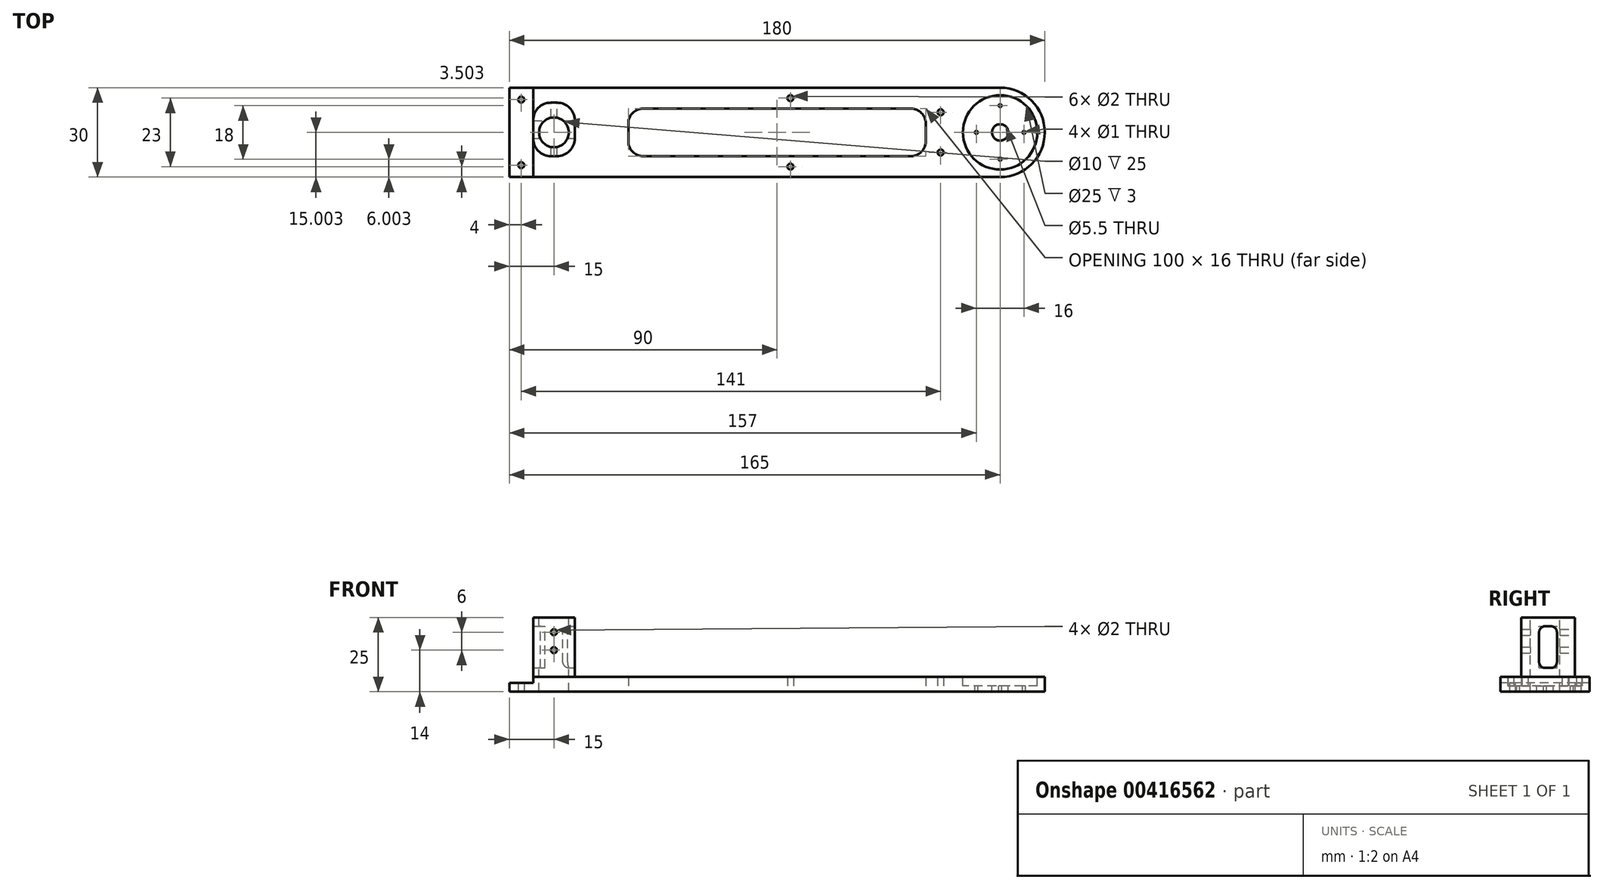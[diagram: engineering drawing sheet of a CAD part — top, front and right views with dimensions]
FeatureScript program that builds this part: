
annotation { "Feature Type Name" : "Feature", "Feature Type Description" : "" }
export const myFeature = defineFeature(function(context is Context, id is Id, definition is map)
    precondition{}
    {
        {
            var Q0;
            Q0=qCreatedBy(makeId("Top.planeOp"),FACE);
            var sketch = newSketch(context, id + "F0", { "sketchPlane" : qUnion([Q0])});
            skLineSegment(sketch, "E0.bottom", {"start": v(-80, 3.1) * mm, "end": v(100, 3.1) * mm});
            skLineSegment(sketch, "E0.top", {"start": v(-80, -26.9) * mm, "end": v(100, -26.9) * mm});
            skLineSegment(sketch, "E0.left", {"start": v(-80, 3.1) * mm, "end": v(-80, -26.9) * mm});
            skLineSegment(sketch, "E0.right", {"start": v(100, 3.1) * mm, "end": v(100, -26.9) * mm});
            skCircle(sketch, "E1", {"center": v(65, -5.15) * mm, "radius": 1 * mm});
            skCircle(sketch, "E2", {"center": v(65, -18.65) * mm, "radius": 1 * mm});
            skLineSegment(sketch, "E3.bottom", {"start": v(-40, -3.9) * mm, "end": v(60, -3.9) * mm});
            skLineSegment(sketch, "E3.top", {"start": v(-40, -19.9) * mm, "end": v(60, -19.9) * mm});
            skLineSegment(sketch, "E3.left", {"start": v(-40, -3.9) * mm, "end": v(-40, -19.9) * mm});
            skLineSegment(sketch, "E3.right", {"start": v(60, -3.9) * mm, "end": v(60, -19.9) * mm});
            skCircle(sketch, "E4", {"center": v(-76, -0.9) * mm, "radius": 1 * mm});
            skCircle(sketch, "E5", {"center": v(-76, -22.9) * mm, "radius": 1 * mm});
            skCircle(sketch, "E6", {"center": v(14.5, -23.4) * mm, "radius": 1 * mm});
            skCircle(sketch, "E7", {"center": v(14.5, -0.4) * mm, "radius": 1 * mm});
            skSolve(sketch);
        }
        {
            var Q0;
            Q0=makeQuery(id+"F0.imprint","IMPRINT",FACE,{"disambiguationData":[TD([[makeQuery(id+"F0.imprint","IMPRINT",EDGE,{"derivedFrom":sQuery(id+"F0.wireOp",EDGE,"E0.bottom")}),-1.0]])]});
            extrude(context, id + "F1", {"entities" : qUnion([Q0]), "depth" : 5 * mm});
        }
        {
            var Q0;
            Q0=makeQuery(id+"F1.opExtrude","CAP_FACE",FACE,{"disambiguationData":[OSD([sQuery(id+"F0.wireOp",EDGE,"E0.bottom"),sQuery(id+"F0.wireOp",EDGE,"E0.top"),sQuery(id+"F0.wireOp",EDGE,"E0.left"),sQuery(id+"F0.wireOp",EDGE,"E0.right")])],"isStart":false});
            var sketch = newSketch(context, id + "F2", { "sketchPlane" : qUnion([Q0])});
            skCircle(sketch, "E8", {"center": v(85, -11.9) * mm, "radius": 12.5 * mm});
            skCircle(sketch, "E9", {"center": v(85, -11.9) * mm, "radius": 2.75 * mm});
            skCircle(sketch, "E10", {"center": v(85, -2.9) * mm, "radius": 0.5 * mm});
            skCircle(sketch, "E11", {"center": v(85, -20.9) * mm, "radius": 0.5 * mm});
            skCircle(sketch, "E12", {"center": v(93, -11.9) * mm, "radius": 0.5 * mm});
            skCircle(sketch, "E13", {"center": v(77, -11.9) * mm, "radius": 0.5 * mm});
            skCircle(sketch, "E14", {"center": v(-65, -11.9) * mm, "radius": 5 * mm});
            skLineSegment(sketch, "E15.bottom", {"start": v(-72, -1.9) * mm, "end": v(-58, -1.9) * mm});
            skLineSegment(sketch, "E15.top", {"start": v(-72, -19.9) * mm, "end": v(-58, -19.9) * mm});
            skLineSegment(sketch, "E15.left", {"start": v(-72, -1.9) * mm, "end": v(-72, -19.9) * mm});
            skLineSegment(sketch, "E15.right", {"start": v(-58, -1.9) * mm, "end": v(-58, -19.9) * mm});
            skLineSegment(sketch, "E16.bottom", {"start": v(-80, 3.1) * mm, "end": v(-72, 3.1) * mm});
            skLineSegment(sketch, "E16.top", {"start": v(-80, -26.9) * mm, "end": v(-72, -26.9) * mm});
            skLineSegment(sketch, "E16.left", {"start": v(-80, 3.1) * mm, "end": v(-80, -26.9) * mm});
            skLineSegment(sketch, "E16.right", {"start": v(-72, 3.1) * mm, "end": v(-72, -26.9) * mm});
            skSolve(sketch);
        }
        {
            var Q0;
            Q0=makeQuery(id+"F2.imprint","IMPRINT",FACE,{"disambiguationData":[TD([[makeQuery(id+"F2.imprint","IMPRINT",EDGE,{"derivedFrom":sQuery(id+"F2.wireOp",EDGE,"E8")}),1.0]])]});
            extrude(context, id + "F3", {"entities" : qUnion([Q0]), "operationType" : NewBodyOperationType.REMOVE, "oppositeDirection" : true, "depth" : 3 * mm});
        }
        {
            var Q0;
            Q0=makeQuery(id+"F2.imprint","IMPRINT",FACE,{"disambiguationData":[TD([[makeQuery(id+"F2.imprint","IMPRINT",EDGE,{"derivedFrom":sQuery(id+"F2.wireOp",EDGE,"E9")}),1.0]])]});
            var Q1;
            Q1=makeQuery(id+"F2.imprint","IMPRINT",FACE,{"disambiguationData":[TD([[makeQuery(id+"F2.imprint","IMPRINT",EDGE,{"derivedFrom":sQuery(id+"F2.wireOp",EDGE,"E10")}),1.0]])]});
            var Q2;
            Q2=makeQuery(id+"F2.imprint","IMPRINT",FACE,{"disambiguationData":[TD([[makeQuery(id+"F2.imprint","IMPRINT",EDGE,{"derivedFrom":sQuery(id+"F2.wireOp",EDGE,"E13")}),1.0]])]});
            var Q3;
            Q3=makeQuery(id+"F2.imprint","IMPRINT",FACE,{"disambiguationData":[TD([[makeQuery(id+"F2.imprint","IMPRINT",EDGE,{"derivedFrom":sQuery(id+"F2.wireOp",EDGE,"E11")}),1.0]])]});
            var Q4;
            Q4=makeQuery(id+"F2.imprint","IMPRINT",FACE,{"disambiguationData":[TD([[makeQuery(id+"F2.imprint","IMPRINT",EDGE,{"derivedFrom":sQuery(id+"F2.wireOp",EDGE,"E12")}),1.0]])]});
            extrude(context, id + "F4", {"entities" : qUnion([Q0, Q1, Q2, Q3, Q4]), "operationType" : NewBodyOperationType.REMOVE, "oppositeDirection" : true, "depth" : 25 * mm});
        }
        {
            var Q0;
            Q0=makeQuery(id+"F1.opExtrude","SWEPT_EDGE",EDGE,{"disambiguationData":[OSD([sQuery(id+"F0.wireOp",EDGE,"E0.bottom"),sQuery(id+"F0.wireOp",EDGE,"E0.right")])]});
            var Q1;
            Q1=makeQuery(id+"F1.opExtrude","SWEPT_EDGE",EDGE,{"disambiguationData":[OSD([sQuery(id+"F0.wireOp",EDGE,"E0.top"),sQuery(id+"F0.wireOp",EDGE,"E0.right")])]});
            fillet(context, id + "F5", {"entities" : qUnion([Q0, Q1]), "radius" : 15 * mm, "tangentPropagation" : true, "allowEdgeOverflow" : false});
        }
        {
            var Q0;
            Q0=makeQuery(id+"F2.imprint","IMPRINT",FACE,{"disambiguationData":[TD([[makeQuery(id+"F2.imprint","IMPRINT",EDGE,{"derivedFrom":sQuery(id+"F2.wireOp",EDGE,"E14")}),1.0]])]});
            extrude(context, id + "F6", {"entities" : qUnion([Q0]), "operationType" : NewBodyOperationType.REMOVE, "oppositeDirection" : true, "depth" : 25 * mm});
        }
        {
            var Q0;
            Q0=makeQuery(id+"F1.opExtrude","SWEPT_EDGE",EDGE,{"disambiguationData":[OSD([sQuery(id+"F0.wireOp",EDGE,"E3.bottom"),sQuery(id+"F0.wireOp",EDGE,"E3.left")])]});
            var Q1;
            Q1=makeQuery(id+"F1.opExtrude","SWEPT_EDGE",EDGE,{"disambiguationData":[OSD([sQuery(id+"F0.wireOp",EDGE,"E3.top"),sQuery(id+"F0.wireOp",EDGE,"E3.left")])]});
            var Q2;
            Q2=makeQuery(id+"F1.opExtrude","SWEPT_EDGE",EDGE,{"disambiguationData":[OSD([sQuery(id+"F0.wireOp",EDGE,"E3.bottom"),sQuery(id+"F0.wireOp",EDGE,"E3.right")])]});
            var Q3;
            Q3=makeQuery(id+"F1.opExtrude","SWEPT_EDGE",EDGE,{"disambiguationData":[OSD([sQuery(id+"F0.wireOp",EDGE,"E3.top"),sQuery(id+"F0.wireOp",EDGE,"E3.right")])]});
            fillet(context, id + "F7", {"entities" : qUnion([Q0, Q1, Q2, Q3]), "radius" : 5 * mm, "tangentPropagation" : true, "allowEdgeOverflow" : false});
        }
        {
            var Q0;
            Q0=makeQuery(id+"F2.imprint","IMPRINT",FACE,{"disambiguationData":[TD([[makeQuery(id+"F2.imprint","IMPRINT",EDGE,{"derivedFrom":sQuery(id+"F2.wireOp",EDGE,"E14")}),-1.0]])]});
            extrude(context, id + "F8", {"entities" : qUnion([Q0]), "operationType" : NewBodyOperationType.ADD, "depth" : 20 * mm, "offsetDistance" : 25 * mm});
        }
        {
            var Q0;
            Q0=makeQuery(id+"F8.opExtrude","SWEPT_EDGE",EDGE,{"disambiguationData":[OSD([sQuery(id+"F2.wireOp",EDGE,"E15.top"),sQuery(id+"F2.wireOp",EDGE,"E15.left")])]});
            var Q1;
            Q1=makeQuery(id+"F8.opExtrude","SWEPT_EDGE",EDGE,{"disambiguationData":[OSD([sQuery(id+"F2.wireOp",EDGE,"E15.top"),sQuery(id+"F2.wireOp",EDGE,"E15.right")])]});
            var Q2;
            Q2=makeQuery(id+"F8.opExtrude","SWEPT_EDGE",EDGE,{"disambiguationData":[OSD([sQuery(id+"F2.wireOp",EDGE,"E15.bottom"),sQuery(id+"F2.wireOp",EDGE,"E15.left")])]});
            var Q3;
            Q3=makeQuery(id+"F8.opExtrude","SWEPT_EDGE",EDGE,{"disambiguationData":[OSD([sQuery(id+"F2.wireOp",EDGE,"E15.bottom"),sQuery(id+"F2.wireOp",EDGE,"E15.right")])]});
            fillet(context, id + "F9", {"entities" : qUnion([Q0, Q1, Q2, Q3]), "radius" : 6 * mm, "tangentPropagation" : true, "allowEdgeOverflow" : false});
        }
        {
            var Q0;
            {var subQ2=sQuery(id+"F2.wireOp",EDGE,"E16.bottom");Q0=makeQuery(id+"F2.imprint","IMPRINT",FACE,{"disambiguationData":[TD([[makeQuery(id+"F2.imprint","IMPRINT",EDGE,{"derivedFrom":subQ2}),-1.0]])]});}
            extrude(context, id + "F10", {"entities" : qUnion([Q0]), "operationType" : NewBodyOperationType.REMOVE, "oppositeDirection" : true, "depth" : 2 * mm, "offsetDistance" : 25 * mm});
        }
        {
            var Q0;
            Q0=makeQuery(id+"F8.opExtrude","SWEPT_FACE",FACE,{"disambiguationData":[OSD([sQuery(id+"F2.wireOp",EDGE,"E15.right")])]});
            var sketch = newSketch(context, id + "F11", { "sketchPlane" : qUnion([Q0])});
            skLineSegment(sketch, "E17.bottom", {"start": v(-13.9, 22) * mm, "end": v(-7.9, 22) * mm});
            skLineSegment(sketch, "E17.top", {"start": v(-13.9, 8) * mm, "end": v(-7.9, 8) * mm});
            skLineSegment(sketch, "E17.left", {"start": v(-13.9, 22) * mm, "end": v(-13.9, 8) * mm});
            skLineSegment(sketch, "E17.right", {"start": v(-7.9, 22) * mm, "end": v(-7.9, 8) * mm});
            skSolve(sketch);
        }
        {
            var Q0;
            Q0=makeQuery(id+"F11.imprint","IMPRINT",FACE,{"disambiguationData":[TD([[makeQuery(id+"F11.imprint","IMPRINT",EDGE,{"derivedFrom":sQuery(id+"F11.wireOp",EDGE,"E17.bottom")}),-1.0]])]});
            extrude(context, id + "F12", {"entities" : qUnion([Q0]), "operationType" : NewBodyOperationType.REMOVE, "oppositeDirection" : true, "depth" : 25 * mm, "offsetDistance" : 25 * mm});
        }
        {
            var Q0;
            {var subQ0=sQuery(id+"F2.wireOp",EDGE,"E15.right");var subQ1=sQuery(id+"F2.wireOp",EDGE,"E15.top");var subQ3=sQuery(id+"F11.wireOp",EDGE,"E17.top");var subQ4=sQuery(id+"F11.wireOp",EDGE,"E17.left");Q0=makeQuery(id+"F12.boolean.opBoolean","COPY",EDGE,{"disambiguationData":[TD([makeQuery(id+"F8.opExtrude","SWEPT_FACE",FACE,{"disambiguationData":[OSD([subQ0])]})])],"derivedFrom":makeQuery(id+"F12.opExtrude","SWEPT_EDGE",EDGE,{"disambiguationData":[OSD([subQ1,subQ0,subQ3,subQ4])]})});}
            var Q1;
            {var subQ0=sQuery(id+"F2.wireOp",EDGE,"E15.right");var subQ2=sQuery(id+"F2.wireOp",EDGE,"E15.bottom");var subQ3=sQuery(id+"F11.wireOp",EDGE,"E17.top");var subQ4=sQuery(id+"F11.wireOp",EDGE,"E17.right");Q1=makeQuery(id+"F12.boolean.opBoolean","COPY",EDGE,{"disambiguationData":[TD([makeQuery(id+"F8.opExtrude","SWEPT_FACE",FACE,{"disambiguationData":[OSD([subQ0])]})])],"derivedFrom":makeQuery(id+"F12.opExtrude","SWEPT_EDGE",EDGE,{"disambiguationData":[OSD([subQ2,subQ0,subQ3,subQ4])]})});}
            var Q2;
            {var subQ0=sQuery(id+"F2.wireOp",EDGE,"E15.right");var subQ2=sQuery(id+"F2.wireOp",EDGE,"E15.bottom");var subQ3=sQuery(id+"F11.wireOp",EDGE,"E17.bottom");var subQ4=sQuery(id+"F11.wireOp",EDGE,"E17.right");Q2=makeQuery(id+"F12.boolean.opBoolean","COPY",EDGE,{"disambiguationData":[TD([makeQuery(id+"F8.opExtrude","SWEPT_FACE",FACE,{"disambiguationData":[OSD([subQ0])]})])],"derivedFrom":makeQuery(id+"F12.opExtrude","SWEPT_EDGE",EDGE,{"disambiguationData":[OSD([subQ2,subQ0,subQ3,subQ4])]})});}
            var Q3;
            {var subQ0=sQuery(id+"F2.wireOp",EDGE,"E15.right");var subQ1=sQuery(id+"F2.wireOp",EDGE,"E15.top");var subQ3=sQuery(id+"F11.wireOp",EDGE,"E17.bottom");var subQ4=sQuery(id+"F11.wireOp",EDGE,"E17.left");Q3=makeQuery(id+"F12.boolean.opBoolean","COPY",EDGE,{"disambiguationData":[TD([makeQuery(id+"F8.opExtrude","SWEPT_FACE",FACE,{"disambiguationData":[OSD([subQ0])]})])],"derivedFrom":makeQuery(id+"F12.opExtrude","SWEPT_EDGE",EDGE,{"disambiguationData":[OSD([subQ1,subQ0,subQ3,subQ4])]})});}
            var Q4;
            {var subQ0=sQuery(id+"F2.wireOp",EDGE,"E16.right");var subQ1=sQuery(id+"F2.wireOp",EDGE,"E15.top");var subQ2=sQuery(id+"F11.wireOp",EDGE,"E17.top");var subQ4=sQuery(id+"F11.wireOp",EDGE,"E17.left");Q4=makeQuery(id+"F12.boolean.opBoolean","COPY",EDGE,{"disambiguationData":[TD([makeQuery(id+"F8.opExtrude","SWEPT_FACE",FACE,{"disambiguationData":[OSD([subQ0])]})])],"derivedFrom":makeQuery(id+"F12.opExtrude","SWEPT_EDGE",EDGE,{"disambiguationData":[OSD([subQ1,sQuery(id+"F2.wireOp",EDGE,"E15.right"),subQ2,subQ4])]})});}
            var Q5;
            {var subQ0=sQuery(id+"F2.wireOp",EDGE,"E16.right");var subQ1=sQuery(id+"F2.wireOp",EDGE,"E15.bottom");var subQ2=sQuery(id+"F11.wireOp",EDGE,"E17.right");var subQ3=sQuery(id+"F11.wireOp",EDGE,"E17.top");Q5=makeQuery(id+"F12.boolean.opBoolean","COPY",EDGE,{"disambiguationData":[TD([makeQuery(id+"F8.opExtrude","SWEPT_FACE",FACE,{"disambiguationData":[OSD([subQ0])]})])],"derivedFrom":makeQuery(id+"F12.opExtrude","SWEPT_EDGE",EDGE,{"disambiguationData":[OSD([subQ1,sQuery(id+"F2.wireOp",EDGE,"E15.right"),subQ3,subQ2])]})});}
            var Q6;
            {var subQ0=sQuery(id+"F2.wireOp",EDGE,"E16.right");var subQ1=sQuery(id+"F2.wireOp",EDGE,"E15.bottom");var subQ2=sQuery(id+"F11.wireOp",EDGE,"E17.right");var subQ4=sQuery(id+"F11.wireOp",EDGE,"E17.bottom");Q6=makeQuery(id+"F12.boolean.opBoolean","COPY",EDGE,{"disambiguationData":[TD([makeQuery(id+"F8.opExtrude","SWEPT_FACE",FACE,{"disambiguationData":[OSD([subQ0])]})])],"derivedFrom":makeQuery(id+"F12.opExtrude","SWEPT_EDGE",EDGE,{"disambiguationData":[OSD([subQ1,sQuery(id+"F2.wireOp",EDGE,"E15.right"),subQ4,subQ2])]})});}
            var Q7;
            {var subQ0=sQuery(id+"F2.wireOp",EDGE,"E16.right");var subQ1=sQuery(id+"F2.wireOp",EDGE,"E15.top");var subQ3=sQuery(id+"F11.wireOp",EDGE,"E17.bottom");var subQ4=sQuery(id+"F11.wireOp",EDGE,"E17.left");Q7=makeQuery(id+"F12.boolean.opBoolean","COPY",EDGE,{"disambiguationData":[TD([makeQuery(id+"F8.opExtrude","SWEPT_FACE",FACE,{"disambiguationData":[OSD([subQ0])]})])],"derivedFrom":makeQuery(id+"F12.opExtrude","SWEPT_EDGE",EDGE,{"disambiguationData":[OSD([subQ1,sQuery(id+"F2.wireOp",EDGE,"E15.right"),subQ3,subQ4])]})});}
            fillet(context, id + "F13", {"entities" : qUnion([Q0, Q1, Q2, Q3, Q4, Q5, Q6, Q7]), "radius" : 2 * mm, "tangentPropagation" : true, "allowEdgeOverflow" : false});
        }
        {
            var Q0;
            Q0=makeQuery(id+"F8.opExtrude","SWEPT_FACE",FACE,{"disambiguationData":[OSD([sQuery(id+"F2.wireOp",EDGE,"E15.bottom")])]});
            var sketch = newSketch(context, id + "F14", { "sketchPlane" : qUnion([Q0])});
            skCircle(sketch, "E18", {"center": v(65, 20) * mm, "radius": 1 * mm});
            skCircle(sketch, "E19", {"center": v(65, 14) * mm, "radius": 1 * mm});
            skSolve(sketch);
        }
        {
            var Q0;
            {var subQ0=sQuery(id+"F14.wireOp",EDGE,"E18");var subQ1=sQuery(id+"F2.wireOp",EDGE,"E15.bottom");var subQ2=makeQuery(id+"F8.opExtrude","SWEPT_FACE",FACE,{"disambiguationData":[OSD([subQ1])]});var subQ3=makeQuery(id+"F14.imprint","INTERSECT",VERTEX,{"derivedFrom":[makeQuery(id+"F9.opFillet","BLEND_EDGE",EDGE,{"blendedFrom":[makeQuery(id+"F8.opExtrude","SWEPT_EDGE",EDGE,{"disambiguationData":[OSD([subQ1,sQuery(id+"F2.wireOp",EDGE,"E16.right")])]}),subQ2],"blendedInto":[subQ2]}),subQ0]});Q0=makeQuery(id+"F14.imprint","IMPRINT",FACE,{"disambiguationData":[TD([[makeQuery(id+"F14.imprint","IMPRINT",EDGE,{"disambiguationData":[TD([[subQ3,-1.0]])],"derivedFrom":subQ0}),1.0]])]});}
            var Q1;
            {var subQ0=sQuery(id+"F14.wireOp",EDGE,"E19");var subQ1=sQuery(id+"F2.wireOp",EDGE,"E15.bottom");var subQ2=makeQuery(id+"F8.opExtrude","SWEPT_FACE",FACE,{"disambiguationData":[OSD([subQ1])]});var subQ3=makeQuery(id+"F14.imprint","INTERSECT",VERTEX,{"derivedFrom":[makeQuery(id+"F9.opFillet","BLEND_EDGE",EDGE,{"blendedFrom":[makeQuery(id+"F8.opExtrude","SWEPT_EDGE",EDGE,{"disambiguationData":[OSD([subQ1,sQuery(id+"F2.wireOp",EDGE,"E16.right")])]}),subQ2],"blendedInto":[subQ2]}),subQ0]});Q1=makeQuery(id+"F14.imprint","IMPRINT",FACE,{"disambiguationData":[TD([[makeQuery(id+"F14.imprint","IMPRINT",EDGE,{"disambiguationData":[TD([[subQ3,-1.0]])],"derivedFrom":subQ0}),1.0]])]});}
            extrude(context, id + "F15", {"entities" : qUnion([Q0, Q1]), "operationType" : NewBodyOperationType.REMOVE, "oppositeDirection" : true, "depth" : 25 * mm, "offsetDistance" : 25 * mm});
        }
    });
